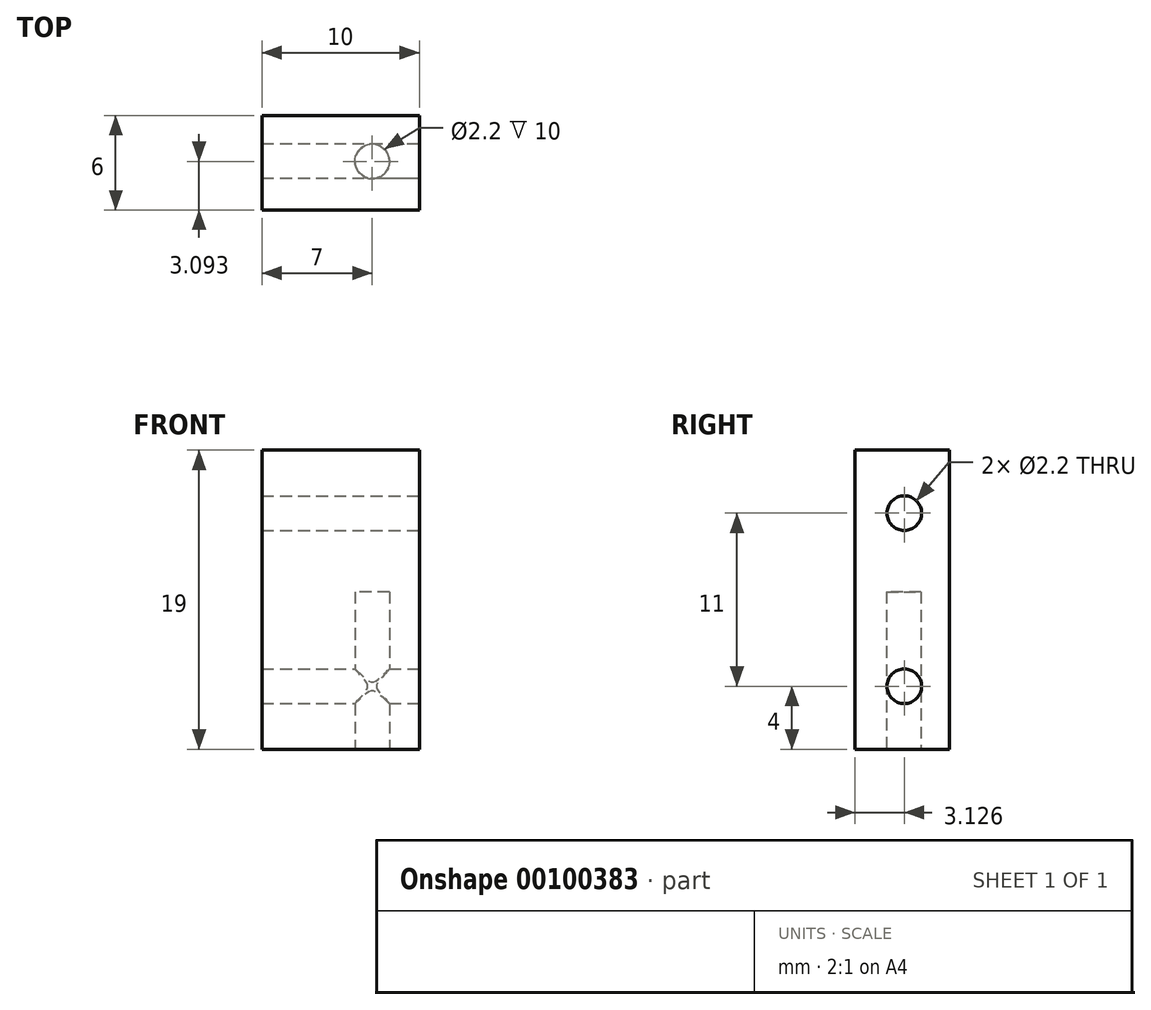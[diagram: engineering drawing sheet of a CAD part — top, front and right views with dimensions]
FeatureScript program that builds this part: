
annotation { "Feature Type Name" : "Feature", "Feature Type Description" : "" }
export const myFeature = defineFeature(function(context is Context, id is Id, definition is map)
    precondition{}
    {
        {
            var Q0;
            Q0=qCreatedBy(makeId("Front.planeOp"),FACE);
            var sketch = newSketch(context, id + "F0", { "sketchPlane" : qUnion([Q0])});
            skLineSegment(sketch, "E0.bottom", {"start": v(0, 19) * mm, "end": v(10, 19) * mm});
            skLineSegment(sketch, "E0.top", {"start": v(0, 0) * mm, "end": v(10, 0) * mm});
            skLineSegment(sketch, "E0.left", {"start": v(0, 19) * mm, "end": v(0, 0) * mm});
            skLineSegment(sketch, "E0.right", {"start": v(10, 19) * mm, "end": v(10, 0) * mm});
            skSolve(sketch);
        }
        {
            var Q0;
            Q0=makeQuery(id+"F0.imprint","IMPRINT",FACE,{"disambiguationData":[TD([[makeQuery(id+"F0.imprint","IMPRINT",EDGE,{"derivedFrom":sQuery(id+"F0.wireOp",EDGE,"E0.bottom")}),-1.0]])]});
            extrude(context, id + "F1", {"entities" : qUnion([Q0]), "depth" : 6 * mm});
        }
        {
            var Q0;
            Q0=makeQuery(id+"F1.opExtrude","SWEPT_FACE",FACE,{"disambiguationData":[OSD([sQuery(id+"F0.wireOp",EDGE,"E0.right")])]});
            var sketch = newSketch(context, id + "F2", { "sketchPlane" : qUnion([Q0])});
            skCircle(sketch, "E1", {"center": v(-2.87, 4) * mm, "radius": 1.1 * mm});
            skCircle(sketch, "E2", {"center": v(-2.87, 15) * mm, "radius": 1.1 * mm});
            skSolve(sketch);
        }
        {
            var Q0;
            Q0 = qSketchRegion(id + "F2", true);
            extrude(context, id + "F3", {"entities" : qUnion([Q0]), "operationType" : NewBodyOperationType.REMOVE, "oppositeDirection" : true, "depth" : 10 * mm});
        }
        {
            var Q0;
            Q0=qCreatedBy(makeId("Top.planeOp"),FACE);
            var sketch = newSketch(context, id + "F4", { "sketchPlane" : qUnion([Q0])});
            skCircle(sketch, "E3", {"center": v(7, -2.9) * mm, "radius": 1.1 * mm});
            skSolve(sketch);
        }
        {
            var Q0;
            Q0=makeQuery(id+"F4.imprint","IMPRINT",FACE,{"disambiguationData":[TD([[makeQuery(id+"F4.imprint","IMPRINT",EDGE,{"derivedFrom":sQuery(id+"F4.wireOp",EDGE,"E3")}),1.0]])]});
            extrude(context, id + "F5", {"entities" : qUnion([Q0]), "operationType" : NewBodyOperationType.REMOVE, "depth" : 10 * mm});
        }
    });
